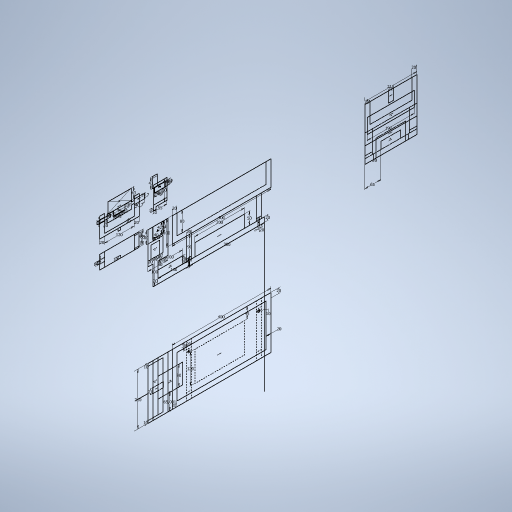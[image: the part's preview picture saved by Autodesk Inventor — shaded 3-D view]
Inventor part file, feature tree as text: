
AUTODESK INVENTOR PART (.ipt)
format: ipt  version: 2023 (Build 270158000, 158)  size: 437,248 bytes
history: native  units: mm
features: sketch x1
ambient origin geometry x8: Origin, YZ Plane, XZ Plane, XY Plane, X Axis, Y Axis, Z Axis, Center Point
feature tree (1):
  sketch  "Boceto1"  dims[d0=130.0mm d2=300.0mm d3=20.0mm d4=20.0mm d5=29.0mm d6=100.0mm d7=20.0mm d9=50.0mm d10=200.0mm d12=5.0mm d15=5.0mm d16=20.0mm d17=100.0mm d18=20.0mm d19=20.0mm d21=20.0mm d22=40.0mm d25=35.0mm d26=80.0mm d28=50.0mm d30=43.0mm d31=43.0mm d32=42.9mm d33=40.7mm d34=10.0mm d35=10.0mm d37=18.0mm d38=55.0mm d39=43.0mm d41=19.7mm d42=40.7mm d43=55.0mm d47=45.0mm d52=21.0mm d55=80.0mm d56=120.0mm d58=20.0mm d59=20.0mm d60=19.7mm d61=40.7mm d78=10.0mm d79=18.0mm d80=45.0mm d81=15.0mm d82=10.0mm d84=20.0mm d85=46.0mm d86=43.0mm d87=94.0mm d88=2.0mm d89=2.0mm d90=10.0mm d91=15.0mm d92=10.0mm d94=10.0mm d95=10.0mm d96=90.0mm d97=20.0mm d98=10.0mm d102=400.0mm d103=100.0mm d104=20.0mm d105=80.0mm d106=400.0mm d107=20.0mm d108=210.0mm d110=10.0mm d111=10.0mm d113=21.0mm d116=80.0mm d119=10.0mm d122=20.0mm d126=120.0mm d129=20.0mm d130=20.0mm d131=210.0mm d134=190.0mm d136=21.0mm d137=30.0mm d141=65.001321mm d142=65.0mm d144=45.0mm d150=10.0mm d152=20.0mm d153=20.0mm d154=55.0mm d156=14.0mm d157=10.0mm d158=45.0mm d159=2.0mm d160=10.0mm]
